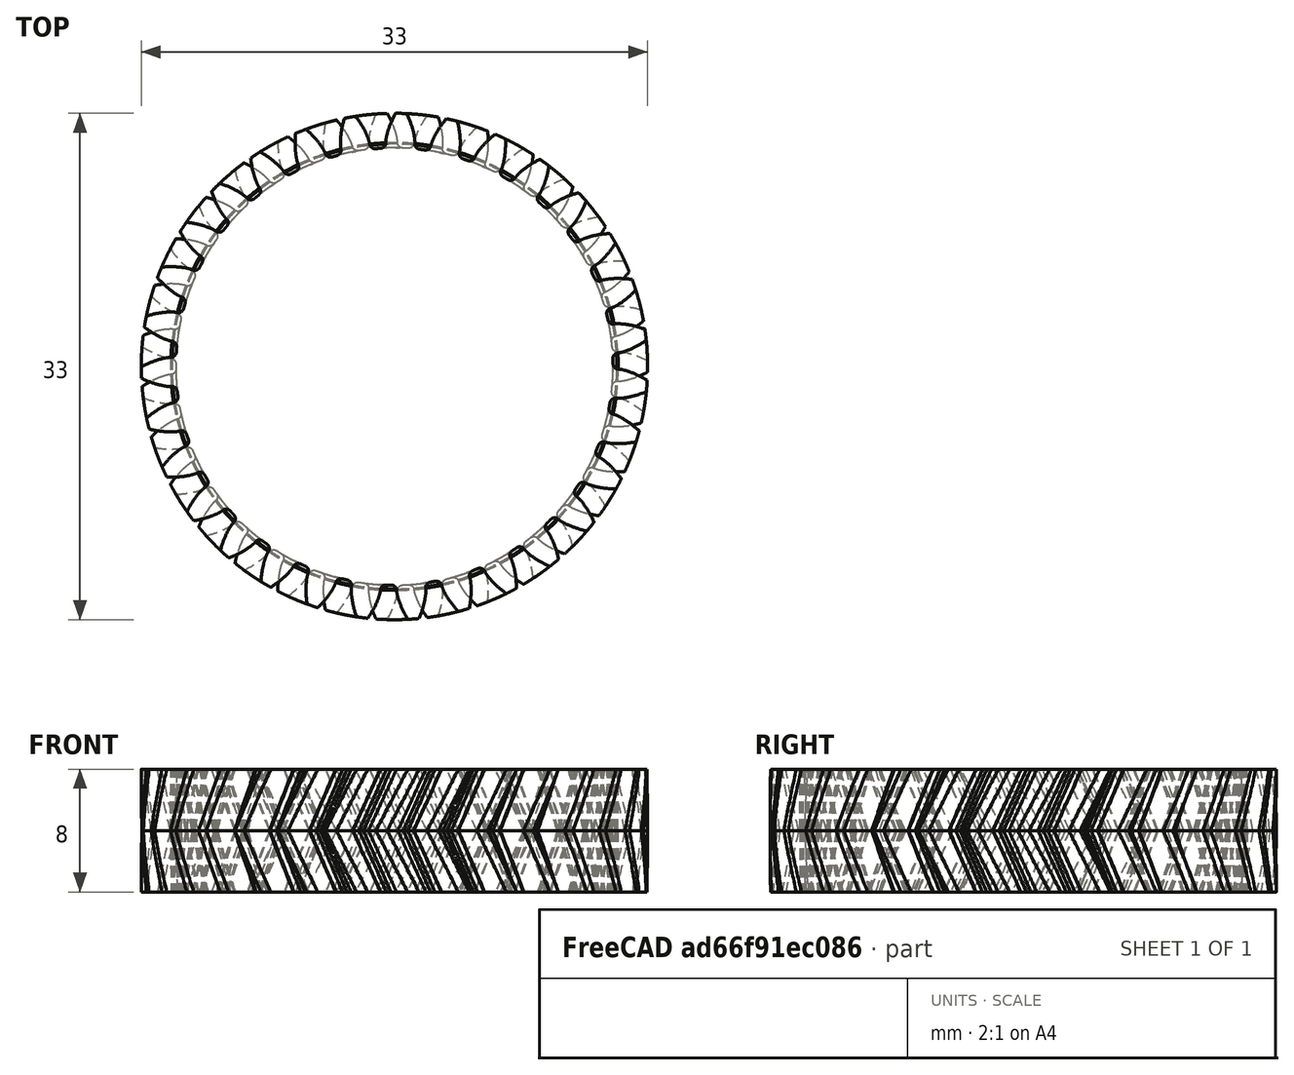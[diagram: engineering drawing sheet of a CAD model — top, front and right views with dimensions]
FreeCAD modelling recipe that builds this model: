
FCSTD DOCUMENT  (FreeCAD 0.17R13541 (Git))
Label: Gear5b
License: All rights reserved
LicenseURL: http://en.wikipedia.org/wiki/All_rights_reserved
objects: Part::Helix×2, Part::Sweep×2, Part::Part2DObjectPython×1
note: 5 computed .brp shape members not serialized (recipe doc carries the construction recipe); baked Part::Feature solids carry a one-line shape summary decoded from their .brp

FEATURE [Part::Part2DObjectPython] InvoluteGear  # Draft 2D object (typed FeaturePython)
  ExternalGear = true
  HighPrecision = true
  Modules = 1
  NumberOfTeeth = 31
  PressureAngle = 20
FEATURE [Part::Helix] Helix002
  Angle = 0
  AttacherType = Attacher::AttachEngine3D
  Height = 4
  LocalCoord = 0
  Pitch = 200
  Radius = 16.5
  Style = 1
FEATURE [Part::Sweep] Sweep
  Frenet = true
  Sections = -> [InvoluteGear]
  Solid = true
  Spine = -> Helix002 [Edge1]
  Transition = 1
FEATURE [Part::Helix] Helix
  Angle = 0
  AttacherType = Attacher::AttachEngine3D
  Height = 4
  LocalCoord = 1
  Pitch = 200
  Placement = pos=(0,0,0) rot=(1,0,0;3.14159rad)
  Radius = 16.5
  Style = 1
FEATURE [Part::Sweep] Sweep001
  Frenet = true
  Sections = -> [InvoluteGear]
  Solid = true
  Spine = -> Helix [Edge1]
  Transition = 1
